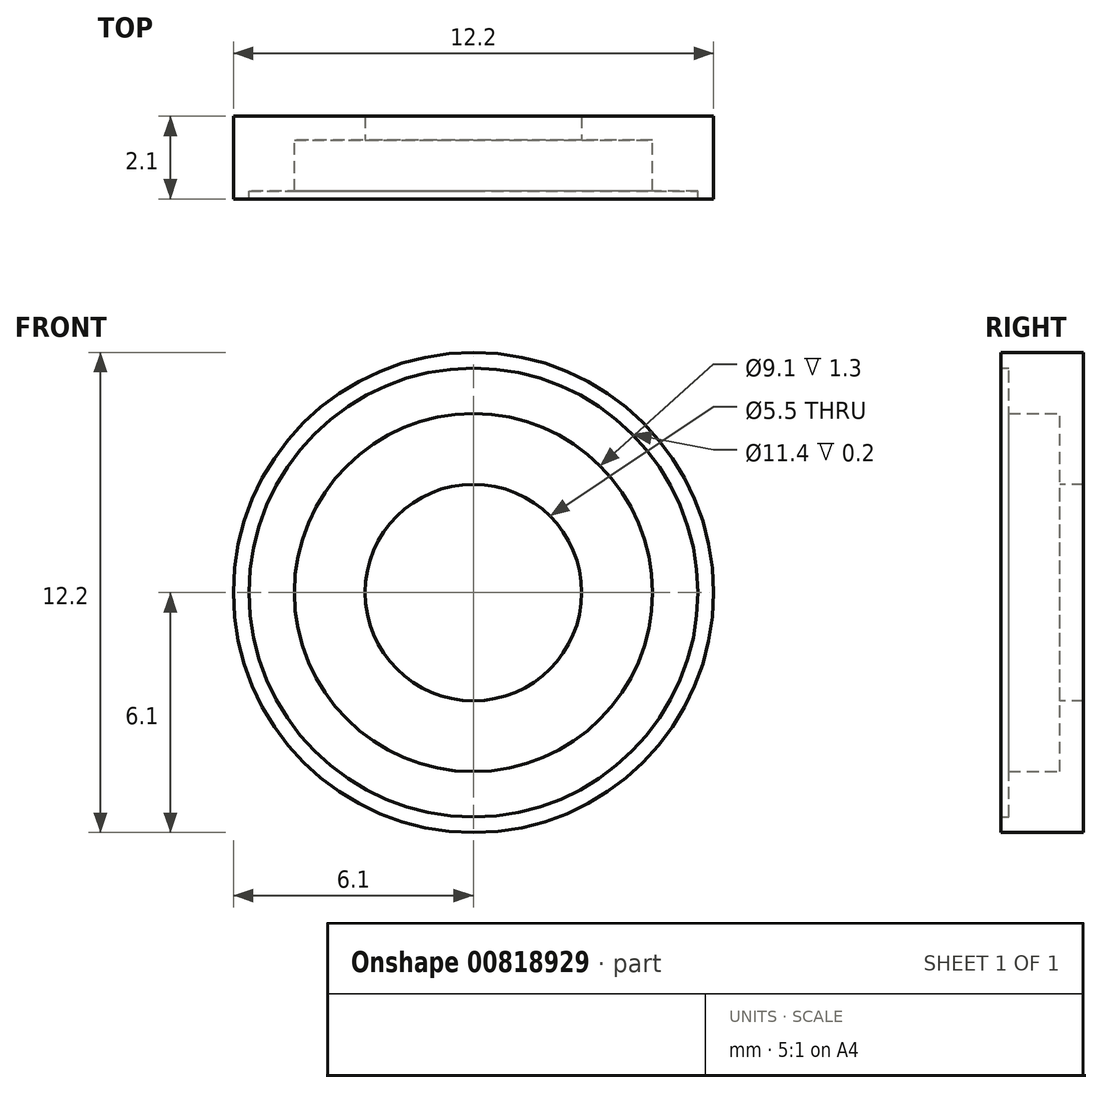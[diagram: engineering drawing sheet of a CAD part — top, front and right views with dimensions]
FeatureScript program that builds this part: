
annotation { "Feature Type Name" : "Feature", "Feature Type Description" : "" }
export const myFeature = defineFeature(function(context is Context, id is Id, definition is map)
    precondition{}
    {
        {
            var Q0;
            Q0=qCreatedBy(makeId("Front.planeOp"),FACE);
            var sketch = newSketch(context, id + "F0", { "sketchPlane" : qUnion([Q0])});
            skCircle(sketch, "E0", {"center": v(0, 0) * mm, "radius": 6.1 * mm});
            skSolve(sketch);
        }
        {
            var Q0;
            Q0=makeQuery(id+"F0.imprint","IMPRINT",FACE,{"disambiguationData":[TD([[makeQuery(id+"F0.imprint","IMPRINT",EDGE,{"derivedFrom":sQuery(id+"F0.wireOp",EDGE,"E0")}),1.0]])]});
            extrude(context, id + "F1", {"entities" : qUnion([Q0]), "depth" : 0.6 * mm, "offsetDistance" : 25 * mm});
        }
        {
            var Q0;
            Q0=makeQuery(id+"F1.opExtrude","CAP_FACE",FACE,{"disambiguationData":[OSD([sQuery(id+"F0.wireOp",EDGE,"E0")])],"isStart":false});
            var sketch = newSketch(context, id + "F2", { "sketchPlane" : qUnion([Q0])});
            skCircle(sketch, "E1", {"center": v(0, 0) * mm, "radius": 6.1 * mm});
            skCircle(sketch, "E2", {"center": v(0, 0) * mm, "radius": 4.55 * mm});
            skSolve(sketch);
        }
        {
            var Q0;
            Q0=makeQuery(id+"F2.imprint","IMPRINT",FACE,{"disambiguationData":[TD([[makeQuery(id+"F2.imprint","IMPRINT",EDGE,{"derivedFrom":sQuery(id+"F2.wireOp",EDGE,"E1")}),1.0]])]});
            extrude(context, id + "F3", {"entities" : qUnion([Q0]), "operationType" : NewBodyOperationType.ADD, "depth" : 1.3 * mm, "offsetDistance" : 25 * mm});
        }
        {
            var Q0;
            Q0=makeQuery(id+"F1.opExtrude","CAP_FACE",FACE,{"disambiguationData":[OSD([sQuery(id+"F0.wireOp",EDGE,"E0")])],"isStart":false});
            var sketch = newSketch(context, id + "F4", { "sketchPlane" : qUnion([Q0])});
            skCircle(sketch, "E3", {"center": v(0, 0) * mm, "radius": 2.75 * mm});
            skSolve(sketch);
        }
        {
            var Q0;
            Q0=makeQuery(id+"F4.imprint","IMPRINT",FACE,{"disambiguationData":[TD([[makeQuery(id+"F4.imprint","IMPRINT",EDGE,{"derivedFrom":sQuery(id+"F4.wireOp",EDGE,"E3")}),1.0]])]});
            extrude(context, id + "F5", {"entities" : qUnion([Q0]), "operationType" : NewBodyOperationType.REMOVE, "oppositeDirection" : true, "depth" : 0.6 * mm, "offsetDistance" : 25 * mm});
        }
        {
            var Q0;
            Q0=makeQuery(id+"F3.opExtrude","CAP_FACE",FACE,{"disambiguationData":[OSD([sQuery(id+"F2.wireOp",EDGE,"E1"),sQuery(id+"F2.wireOp",EDGE,"E2")])],"isStart":false});
            var sketch = newSketch(context, id + "F6", { "sketchPlane" : qUnion([Q0])});
            skCircle(sketch, "E4", {"center": v(0, 0) * mm, "radius": 6.1 * mm});
            skCircle(sketch, "E5", {"center": v(0, 0) * mm, "radius": 5.7 * mm});
            skSolve(sketch);
        }
        {
            var Q0;
            Q0=makeQuery(id+"F6.imprint","IMPRINT",FACE,{"disambiguationData":[TD([[makeQuery(id+"F6.imprint","IMPRINT",EDGE,{"derivedFrom":sQuery(id+"F6.wireOp",EDGE,"E4")}),1.0]])]});
            extrude(context, id + "F7", {"entities" : qUnion([Q0]), "operationType" : NewBodyOperationType.ADD, "depth" : 0.2 * mm, "offsetDistance" : 25 * mm});
        }
    });
